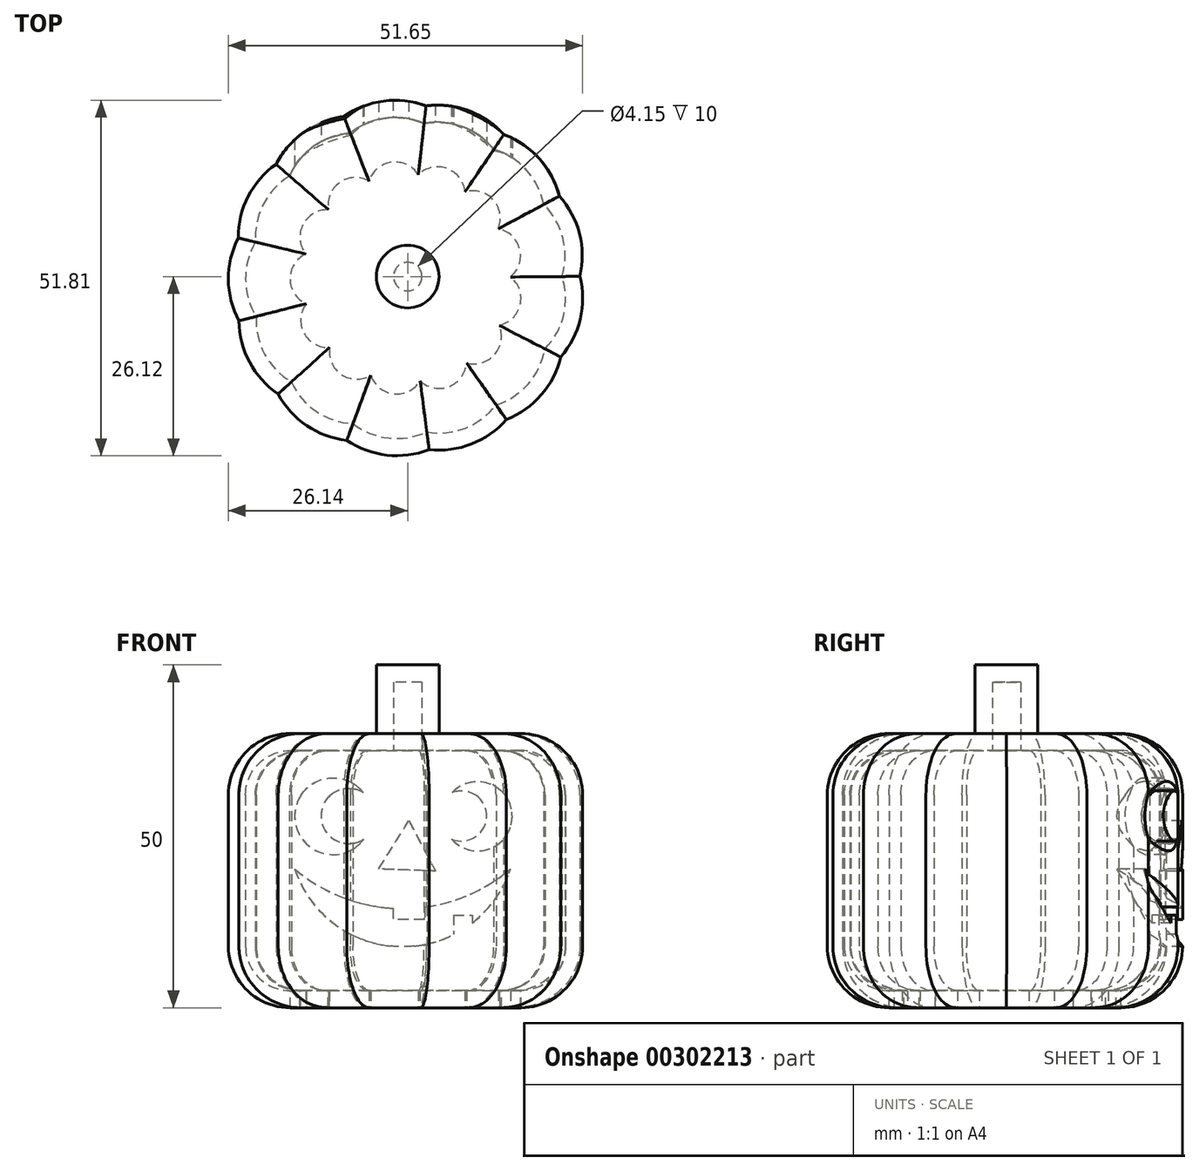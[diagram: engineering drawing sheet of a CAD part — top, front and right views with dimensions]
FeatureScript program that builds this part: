
annotation { "Feature Type Name" : "Feature", "Feature Type Description" : "" }
export const myFeature = defineFeature(function(context is Context, id is Id, definition is map)
    precondition{}
    {
        {
            var Q0;
            Q0=qCreatedBy(makeId("Top.planeOp"),FACE);
            var sketch = newSketch(context, id + "F0", { "sketchPlane" : qUnion([Q0])});
            skArc(sketch, "E0", {"start": v(2.68, 24.88) * mm, "mid": v(-3.5, 25.58) * mm, "end": v(-9.3, 23.32) * mm});
            skArc(sketch, "E1", {"start": v(-9.3, 23.32) * mm, "mid": v(-15.1, 21.06) * mm, "end": v(-19.18, 16.37) * mm});
            skArc(sketch, "E2", {"start": v(-19.18, 16.37) * mm, "mid": v(-23.27, 11.67) * mm, "end": v(-24.7, 5.62) * mm});
            skArc(sketch, "E3", {"start": v(-24.7, 5.62) * mm, "mid": v(-26.14, -0.43) * mm, "end": v(-24.6, -6.46) * mm});
            skArc(sketch, "E4", {"start": v(-24.6, -6.46) * mm, "mid": v(-23.05, -12.5) * mm, "end": v(-18.88, -17.11) * mm});
            skArc(sketch, "E5", {"start": v(-18.88, -17.11) * mm, "mid": v(-14.72, -21.73) * mm, "end": v(-8.88, -23.89) * mm});
            skArc(sketch, "E6", {"start": v(-8.88, -23.89) * mm, "mid": v(-3.04, -26.04) * mm, "end": v(3.13, -25.23) * mm});
            skArc(sketch, "E7", {"start": v(3.13, -25.23) * mm, "mid": v(9.3, -24.43) * mm, "end": v(14.39, -20.85) * mm});
            skArc(sketch, "E8", {"start": v(14.39, -20.85) * mm, "mid": v(19.48, -17.27) * mm, "end": v(22.32, -11.73) * mm});
            skArc(sketch, "E9", {"start": v(22.32, -11.73) * mm, "mid": v(25.16, -6.2) * mm, "end": v(25.1, 0.02) * mm});
            skArc(sketch, "E10", {"start": v(14.02, 20.7) * mm, "mid": v(8.87, 24.19) * mm, "end": v(2.68, 24.88) * mm});
            skArc(sketch, "E11", {"start": v(22.11, 11.73) * mm, "mid": v(19.17, 17.21) * mm, "end": v(14.02, 20.7) * mm});
            skArc(sketch, "E12", {"start": v(25.1, 0.02) * mm, "mid": v(25.05, 6.24) * mm, "end": v(22.11, 11.73) * mm});
            skSolve(sketch);
        }
        {
            var Q0;
            Q0=qSketchRegion(id+"F0",true);
            extrude(context, id + "F1", {"entities" : qUnion([Q0]), "depth" : 40 * mm});
        }
        {
            var Q0;
            Q0=makeQuery(id+"F1.opExtrude","CAP_EDGE",EDGE,{"disambiguationData":[OSD([sQuery(id+"F0.wireOp",EDGE,"E4")])],"isStart":false});
            var Q1;
            Q1=makeQuery(id+"F1.opExtrude","CAP_EDGE",EDGE,{"disambiguationData":[OSD([sQuery(id+"F0.wireOp",EDGE,"E5")])],"isStart":false});
            var Q2;
            Q2=makeQuery(id+"F1.opExtrude","CAP_EDGE",EDGE,{"disambiguationData":[OSD([sQuery(id+"F0.wireOp",EDGE,"E6")])],"isStart":false});
            var Q3;
            Q3=makeQuery(id+"F1.opExtrude","CAP_EDGE",EDGE,{"disambiguationData":[OSD([sQuery(id+"F0.wireOp",EDGE,"E7")])],"isStart":false});
            var Q4;
            Q4=makeQuery(id+"F1.opExtrude","CAP_EDGE",EDGE,{"disambiguationData":[OSD([sQuery(id+"F0.wireOp",EDGE,"E8")])],"isStart":false});
            var Q5;
            Q5=makeQuery(id+"F1.opExtrude","CAP_EDGE",EDGE,{"disambiguationData":[OSD([sQuery(id+"F0.wireOp",EDGE,"E9")])],"isStart":false});
            var Q6;
            Q6=makeQuery(id+"F1.opExtrude","CAP_EDGE",EDGE,{"disambiguationData":[OSD([sQuery(id+"F0.wireOp",EDGE,"E12")])],"isStart":false});
            var Q7;
            Q7=makeQuery(id+"F1.opExtrude","CAP_EDGE",EDGE,{"disambiguationData":[OSD([sQuery(id+"F0.wireOp",EDGE,"E11")])],"isStart":false});
            var Q8;
            Q8=makeQuery(id+"F1.opExtrude","CAP_EDGE",EDGE,{"disambiguationData":[OSD([sQuery(id+"F0.wireOp",EDGE,"E10")])],"isStart":false});
            var Q9;
            Q9=makeQuery(id+"F1.opExtrude","CAP_EDGE",EDGE,{"disambiguationData":[OSD([sQuery(id+"F0.wireOp",EDGE,"E0")])],"isStart":false});
            var Q10;
            Q10=makeQuery(id+"F1.opExtrude","CAP_EDGE",EDGE,{"disambiguationData":[OSD([sQuery(id+"F0.wireOp",EDGE,"E1")])],"isStart":false});
            var Q11;
            Q11=makeQuery(id+"F1.opExtrude","CAP_EDGE",EDGE,{"disambiguationData":[OSD([sQuery(id+"F0.wireOp",EDGE,"E2")])],"isStart":false});
            var Q12;
            Q12=makeQuery(id+"F1.opExtrude","CAP_EDGE",EDGE,{"disambiguationData":[OSD([sQuery(id+"F0.wireOp",EDGE,"E3")])],"isStart":false});
            var Q13;
            Q13=makeQuery(id+"F1.opExtrude","CAP_EDGE",EDGE,{"disambiguationData":[OSD([sQuery(id+"F0.wireOp",EDGE,"E6")])],"isStart":true});
            var Q14;
            Q14=makeQuery(id+"F1.opExtrude","CAP_EDGE",EDGE,{"disambiguationData":[OSD([sQuery(id+"F0.wireOp",EDGE,"E7")])],"isStart":true});
            var Q15;
            Q15=makeQuery(id+"F1.opExtrude","CAP_EDGE",EDGE,{"disambiguationData":[OSD([sQuery(id+"F0.wireOp",EDGE,"E8")])],"isStart":true});
            var Q16;
            Q16=makeQuery(id+"F1.opExtrude","CAP_EDGE",EDGE,{"disambiguationData":[OSD([sQuery(id+"F0.wireOp",EDGE,"E9")])],"isStart":true});
            var Q17;
            Q17=makeQuery(id+"F1.opExtrude","CAP_EDGE",EDGE,{"disambiguationData":[OSD([sQuery(id+"F0.wireOp",EDGE,"E12")])],"isStart":true});
            var Q18;
            Q18=makeQuery(id+"F1.opExtrude","CAP_EDGE",EDGE,{"disambiguationData":[OSD([sQuery(id+"F0.wireOp",EDGE,"E11")])],"isStart":true});
            var Q19;
            Q19=makeQuery(id+"F1.opExtrude","CAP_EDGE",EDGE,{"disambiguationData":[OSD([sQuery(id+"F0.wireOp",EDGE,"E10")])],"isStart":true});
            var Q20;
            Q20=makeQuery(id+"F1.opExtrude","CAP_EDGE",EDGE,{"disambiguationData":[OSD([sQuery(id+"F0.wireOp",EDGE,"E0")])],"isStart":true});
            var Q21;
            Q21=makeQuery(id+"F1.opExtrude","CAP_EDGE",EDGE,{"disambiguationData":[OSD([sQuery(id+"F0.wireOp",EDGE,"E1")])],"isStart":true});
            var Q22;
            Q22=makeQuery(id+"F1.opExtrude","CAP_EDGE",EDGE,{"disambiguationData":[OSD([sQuery(id+"F0.wireOp",EDGE,"E2")])],"isStart":true});
            var Q23;
            Q23=makeQuery(id+"F1.opExtrude","CAP_EDGE",EDGE,{"disambiguationData":[OSD([sQuery(id+"F0.wireOp",EDGE,"E3")])],"isStart":true});
            var Q24;
            Q24=makeQuery(id+"F1.opExtrude","CAP_EDGE",EDGE,{"disambiguationData":[OSD([sQuery(id+"F0.wireOp",EDGE,"E4")])],"isStart":true});
            var Q25;
            Q25=makeQuery(id+"F1.opExtrude","CAP_EDGE",EDGE,{"disambiguationData":[OSD([sQuery(id+"F0.wireOp",EDGE,"E5")])],"isStart":true});
            fillet(context, id + "F2", {"entities" : qUnion([Q0, Q1, Q2, Q3, Q4, Q5, Q6, Q7, Q8, Q9, Q10, Q11, Q12, Q13, Q14, Q15, Q16, Q17, Q18, Q19, Q20, Q21, Q22, Q23, Q24, Q25]), "radius" : 9 * mm, "tangentPropagation" : true, "allowEdgeOverflow" : false});
        }
        {
            var Q0;
            Q0=makeQuery(id+"F1.opExtrude","CAP_FACE",FACE,{"disambiguationData":[OSD([sQuery(id+"F0.wireOp",EDGE,"E0"),sQuery(id+"F0.wireOp",EDGE,"E1"),sQuery(id+"F0.wireOp",EDGE,"E2"),sQuery(id+"F0.wireOp",EDGE,"E3"),sQuery(id+"F0.wireOp",EDGE,"E4"),sQuery(id+"F0.wireOp",EDGE,"E5"),sQuery(id+"F0.wireOp",EDGE,"E6"),sQuery(id+"F0.wireOp",EDGE,"E7"),sQuery(id+"F0.wireOp",EDGE,"E8"),sQuery(id+"F0.wireOp",EDGE,"E9"),sQuery(id+"F0.wireOp",EDGE,"E10"),sQuery(id+"F0.wireOp",EDGE,"E11"),sQuery(id+"F0.wireOp",EDGE,"E12")])],"isStart":false});
            var sketch = newSketch(context, id + "F3", { "sketchPlane" : qUnion([Q0])});
            skCircle(sketch, "E13", {"center": v(0, 0) * mm, "radius": 4.57 * mm});
            skSolve(sketch);
        }
        {
            var Q0;
            Q0=qSketchRegion(id+"F3",true);
            extrude(context, id + "F4", {"entities" : qUnion([Q0]), "operationType" : NewBodyOperationType.ADD, "depth" : 10 * mm});
        }
        {
            var Q0;
            Q0=makeQuery(id+"F1.opExtrude","CAP_FACE",FACE,{"disambiguationData":[OSD([sQuery(id+"F0.wireOp",EDGE,"E0"),sQuery(id+"F0.wireOp",EDGE,"E1"),sQuery(id+"F0.wireOp",EDGE,"E2"),sQuery(id+"F0.wireOp",EDGE,"E3"),sQuery(id+"F0.wireOp",EDGE,"E4"),sQuery(id+"F0.wireOp",EDGE,"E5"),sQuery(id+"F0.wireOp",EDGE,"E6"),sQuery(id+"F0.wireOp",EDGE,"E7"),sQuery(id+"F0.wireOp",EDGE,"E8"),sQuery(id+"F0.wireOp",EDGE,"E9"),sQuery(id+"F0.wireOp",EDGE,"E10"),sQuery(id+"F0.wireOp",EDGE,"E11"),sQuery(id+"F0.wireOp",EDGE,"E12")])],"isStart":true});
            shell(context, id + "F5", {"entities" : qUnion([Q0]), "thickness" : 2.5 * mm});
        }
        {
            var Q0;
            Q0=qCreatedBy(makeId("Front.planeOp"),FACE);
            var sketch = newSketch(context, id + "F6", { "sketchPlane" : qUnion([Q0])});
            skArc(sketch, "E14", {"start": v(-6.5, 31.42) * mm, "mid": v(-12.63, 27.9) * mm, "end": v(-6.37, 24.6) * mm});
            skArc(sketch, "E15", {"start": v(-6.5, 31.42) * mm, "mid": v(-16.47, 27.82) * mm, "end": v(-6.37, 24.6) * mm});
            skArc(sketch, "E16", {"start": v(6.37, 24.6) * mm, "mid": v(11.5, 27.92) * mm, "end": v(6.5, 31.42) * mm});
            skArc(sketch, "E17", {"start": v(6.37, 24.6) * mm, "mid": v(15.24, 27.85) * mm, "end": v(6.5, 31.42) * mm});
            skLineSegment(sketch, "E18.0", {"start": v(4.06, 19.93) * mm, "end": v(-4.23, 20.23) * mm});
            skLineSegment(sketch, "E18.1", {"start": v(-4.23, 20.23) * mm, "end": v(0.17, 27.26) * mm});
            skLineSegment(sketch, "E18.2", {"start": v(0.17, 27.26) * mm, "end": v(4.06, 19.93) * mm});
            skArc(sketch, "E19", {"start": v(-16.47, 20.23) * mm, "mid": v(-0.74, 8.9) * mm, "end": v(15, 20.23) * mm});
            skPoint(sketch, "E19.startSnap0", {"position": v(-16.47, 27.82) * mm});
            skArc(sketch, "E20", {"start": v(-16.47, 20.23) * mm, "mid": v(-0.74, 14.47) * mm, "end": v(15, 20.23) * mm});
            skLineSegment(sketch, "E21.bottom", {"start": v(2.48, 12.86) * mm, "end": v(-2.13, 12.86) * mm});
            skLineSegment(sketch, "E21.top", {"start": v(2.48, 16.12) * mm, "end": v(-2.13, 16.12) * mm});
            skLineSegment(sketch, "E21.left", {"start": v(2.48, 12.86) * mm, "end": v(2.48, 16.12) * mm});
            skLineSegment(sketch, "E21.right", {"start": v(-2.13, 12.86) * mm, "end": v(-2.13, 16.12) * mm});
            skPoint(sketch, "E21.middle", {"position": v(0.17, 14.49) * mm});
            skLineSegment(sketch, "E22.bottom", {"start": v(6.72, 13.53) * mm, "end": v(9.4, 13.53) * mm});
            skLineSegment(sketch, "E22.top", {"start": v(6.72, 9.35) * mm, "end": v(9.4, 9.35) * mm});
            skLineSegment(sketch, "E22.left", {"start": v(6.72, 13.53) * mm, "end": v(6.72, 9.35) * mm});
            skLineSegment(sketch, "E22.right", {"start": v(9.4, 13.53) * mm, "end": v(9.4, 9.35) * mm});
            skPoint(sketch, "E22.middle", {"position": v(8.07, 11.44) * mm});
            skSolve(sketch);
        }
        {
            var Q0;
            Q0=makeQuery(id+"F6.imprint","IMPRINT",FACE,{"disambiguationData":[TD([[makeQuery(id+"F6.imprint","IMPRINT",EDGE,{"derivedFrom":sQuery(id+"F6.wireOp",EDGE,"E18.0")}),-1.0]])]});
            var Q1;
            Q1=makeQuery(id+"F6.imprint","IMPRINT",FACE,{"disambiguationData":[TD([[makeQuery(id+"F6.imprint","IMPRINT",EDGE,{"derivedFrom":sQuery(id+"F6.wireOp",EDGE,"E16")}),-1.0]])]});
            var Q2;
            Q2=makeQuery(id+"F6.imprint","IMPRINT",FACE,{"disambiguationData":[TD([[makeQuery(id+"F6.imprint","IMPRINT",EDGE,{"derivedFrom":sQuery(id+"F6.wireOp",EDGE,"E14")}),-1.0]])]});
            var Q3;
            {var subQ13=sQuery(id+"F6.wireOp",EDGE,"E21.bottom");Q3=makeQuery(id+"F6.imprint","IMPRINT",FACE,{"disambiguationData":[TD([[makeQuery(id+"F6.imprint","IMPRINT",EDGE,{"derivedFrom":subQ13}),1.0]])]});}
            extrude(context, id + "F7", {"entities" : qUnion([Q0, Q1, Q2, Q3]), "operationType" : NewBodyOperationType.REMOVE, "oppositeDirection" : true, "depth" : 100 * mm});
        }
    });
